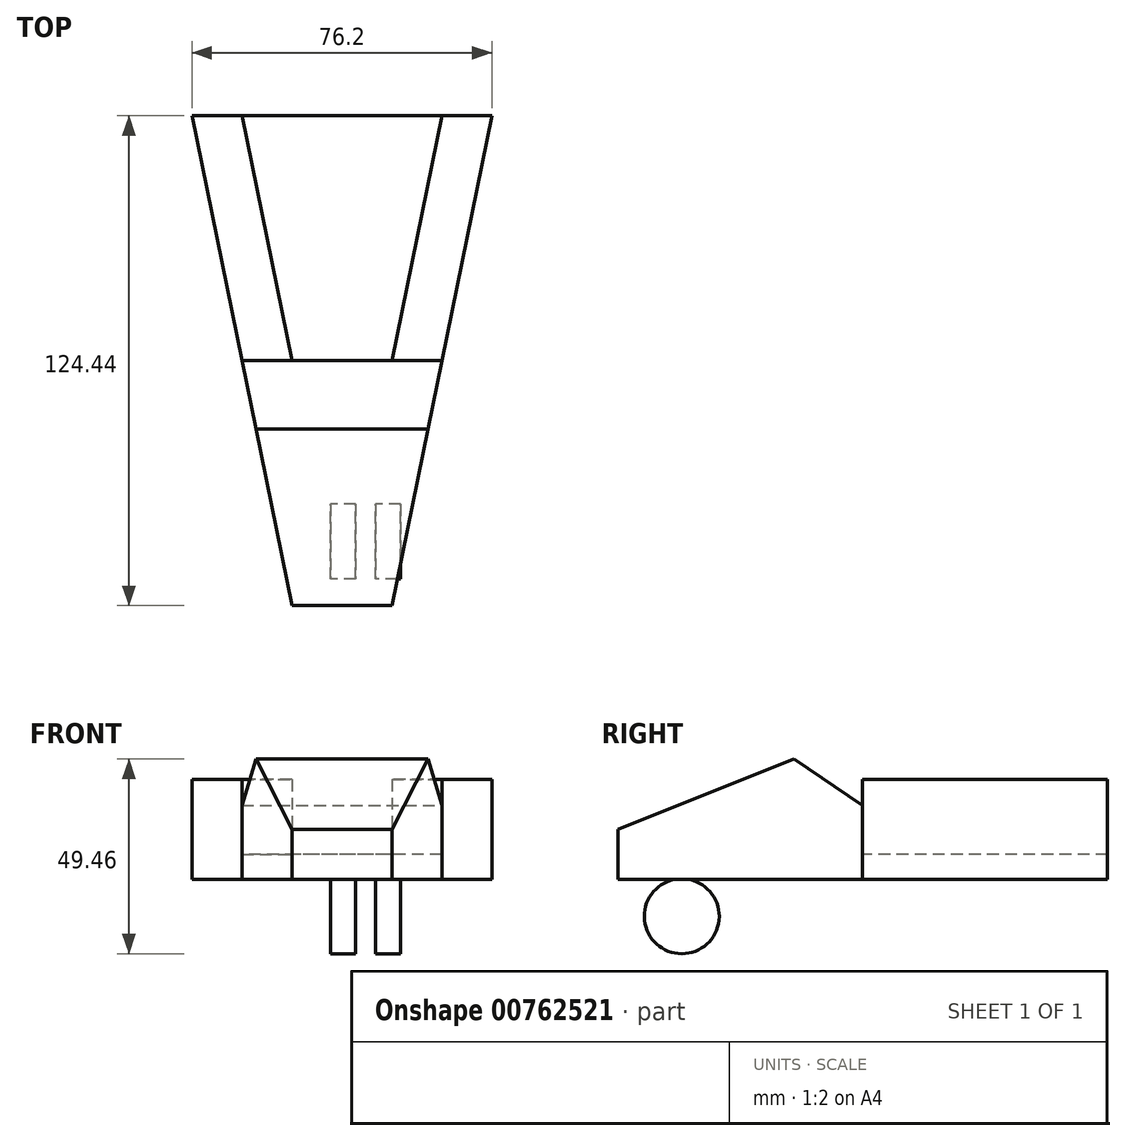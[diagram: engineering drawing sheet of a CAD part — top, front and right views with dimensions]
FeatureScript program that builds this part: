
annotation { "Feature Type Name" : "Feature", "Feature Type Description" : "" }
export const myFeature = defineFeature(function(context is Context, id is Id, definition is map)
    precondition{}
    {
        {
            var Q0;
            Q0=qCreatedBy(makeId("Top.planeOp"),FACE);
            var sketch = newSketch(context, id + "F0", { "sketchPlane" : qUnion([Q0])});
            skLineSegment(sketch, "E0", {"start": v(-13.03, -62.22) * mm, "end": v(12.37, -62.22) * mm});
            skLineSegment(sketch, "E1", {"start": v(12.37, -62.22) * mm, "end": v(37.77, 62.22) * mm});
            skLineSegment(sketch, "E2", {"start": v(37.77, 62.22) * mm, "end": v(-38.43, 62.22) * mm});
            skLineSegment(sketch, "E3", {"start": v(-38.43, 62.22) * mm, "end": v(-13.03, -62.22) * mm});
            skLineSegment(sketch, "E4", {"start": v(-38.43, 62.22) * mm, "end": v(-25.73, 62.22) * mm});
            skLineSegment(sketch, "E5", {"start": v(-25.73, 62.22) * mm, "end": v(-13.03, 0) * mm});
            skLineSegment(sketch, "E6", {"start": v(37.77, 62.22) * mm, "end": v(25.07, 62.22) * mm});
            skLineSegment(sketch, "E7", {"start": v(25.07, 62.22) * mm, "end": v(12.37, 0) * mm});
            skLineSegment(sketch, "E8", {"start": v(12.37, 0) * mm, "end": v(-13.03, 0) * mm});
            skLineSegment(sketch, "E9", {"start": v(-13.03, 0) * mm, "end": v(-25.73, 0) * mm});
            skLineSegment(sketch, "E10", {"start": v(12.37, 0) * mm, "end": v(25.07, 0) * mm});
            skSolve(sketch);
        }
        {
            var Q0;
            {var subQ3=sQuery(id+"F0.wireOp",EDGE,"E5");Q0=makeQuery(id+"F0.imprint","IMPRINT",FACE,{"disambiguationData":[TD([[makeQuery(id+"F0.imprint","IMPRINT",EDGE,{"derivedFrom":subQ3}),-1.0]])]});}
            var Q1;
            {var subQ4=sQuery(id+"F0.wireOp",EDGE,"E7");Q1=makeQuery(id+"F0.imprint","IMPRINT",FACE,{"disambiguationData":[TD([[makeQuery(id+"F0.imprint","IMPRINT",EDGE,{"derivedFrom":subQ4}),1.0]])]});}
            extrude(context, id + "F1", {"entities" : qUnion([Q0, Q1]), "depth" : 25.4 * mm, "offsetDistance" : 25.4 * mm});
        }
        {
            var Q0;
            {var subQ1=sQuery(id+"F0.wireOp",EDGE,"E0");Q0=makeQuery(id+"F0.imprint","IMPRINT",FACE,{"disambiguationData":[TD([[makeQuery(id+"F0.imprint","IMPRINT",EDGE,{"derivedFrom":subQ1}),1.0]])]});}
            extrude(context, id + "F2", {"entities" : qUnion([Q0]), "depth" : 38.1 * mm, "offsetDistance" : 25.4 * mm});
        }
        {
            var Q0;
            {var subQ2=sQuery(id+"F0.wireOp",EDGE,"E5");Q0=makeQuery(id+"F0.imprint","IMPRINT",FACE,{"disambiguationData":[TD([[makeQuery(id+"F0.imprint","IMPRINT",EDGE,{"derivedFrom":subQ2}),1.0]])]});}
            extrude(context, id + "F3", {"entities" : qUnion([Q0]), "depth" : 6.35 * mm, "offsetDistance" : 25.4 * mm});
        }
        {
            var Q0;
            Q0=makeQuery(id+"F2.opExtrude","CAP_EDGE",EDGE,{"disambiguationData":[OSD([sQuery(id+"F0.wireOp",EDGE,"E0")])],"isStart":false});
            chamfer(context, id + "F4", {"entities" : qUnion([Q0]), "chamferType" : ChamferType.TWO_OFFSETS, "width1" : 63.5 * mm, "oppositeDirection" : false, "width2" : 25.4 * mm, "tangentPropagation" : true});
        }
        {
            var Q0;
            Q0=makeQuery(id+"F4.opChamfer","BLEND_EDGE",EDGE,{"blendedFrom":[makeQuery(id+"F2.opExtrude","CAP_EDGE",EDGE,{"disambiguationData":[OSD([sQuery(id+"F0.wireOp",EDGE,"E0")])],"isStart":false}),makeQuery(id+"F2.opExtrude","SWEPT_FACE",FACE,{"disambiguationData":[OSD([sQuery(id+"F0.wireOp",EDGE,"E8"),sQuery(id+"F0.wireOp",EDGE,"E9"),sQuery(id+"F0.wireOp",EDGE,"E10")])]})],"blendedInto":[makeQuery(id+"F2.opExtrude","SWEPT_FACE",FACE,{"disambiguationData":[OSD([sQuery(id+"F0.wireOp",EDGE,"E8"),sQuery(id+"F0.wireOp",EDGE,"E9"),sQuery(id+"F0.wireOp",EDGE,"E10")])]})]});
            chamfer(context, id + "F5", {"entities" : qUnion([Q0]), "width" : 12.7 * mm, "tangentPropagation" : true});
        }
        {
            var Q0;
            Q0=qCreatedBy(makeId("Right.planeOp"),FACE);
            var sketch = newSketch(context, id + "F6", { "sketchPlane" : qUnion([Q0])});
            skCircle(sketch, "E11", {"center": v(-45.96, -9.31) * mm, "radius": 9.53 * mm});
            skSolve(sketch);
        }
        {
            var Q0;
            Q0=makeQuery(id+"F6.imprint","IMPRINT",FACE,{"disambiguationData":[TD([[makeQuery(id+"F6.imprint","IMPRINT",EDGE,{"derivedFrom":sQuery(id+"F6.wireOp",EDGE,"E11")}),1.0]])]});
            extrude(context, id + "F7", {"entities" : qUnion([Q0]), "endBound" : BoundingType.SYMMETRIC, "depth" : 6.35 * mm, "offsetDistance" : 25.4 * mm});
        }
        {
            var Q0;
            Q0=makeQuery(id+"F7.opExtrude","SWEPT_BODY",BODY,{"disambiguationData":[OSD([sQuery(id+"F6.wireOp",EDGE,"E11")])]});
            transform(context, id + "F8", {"entities" : qUnion([Q0]), "transformType" : TransformType.TRANSLATION_3D, "dx" : 11.43 * mm, "dy" : 0 * mm, "dz" : 0 * mm, "makeCopy" : true});
        }
    });
